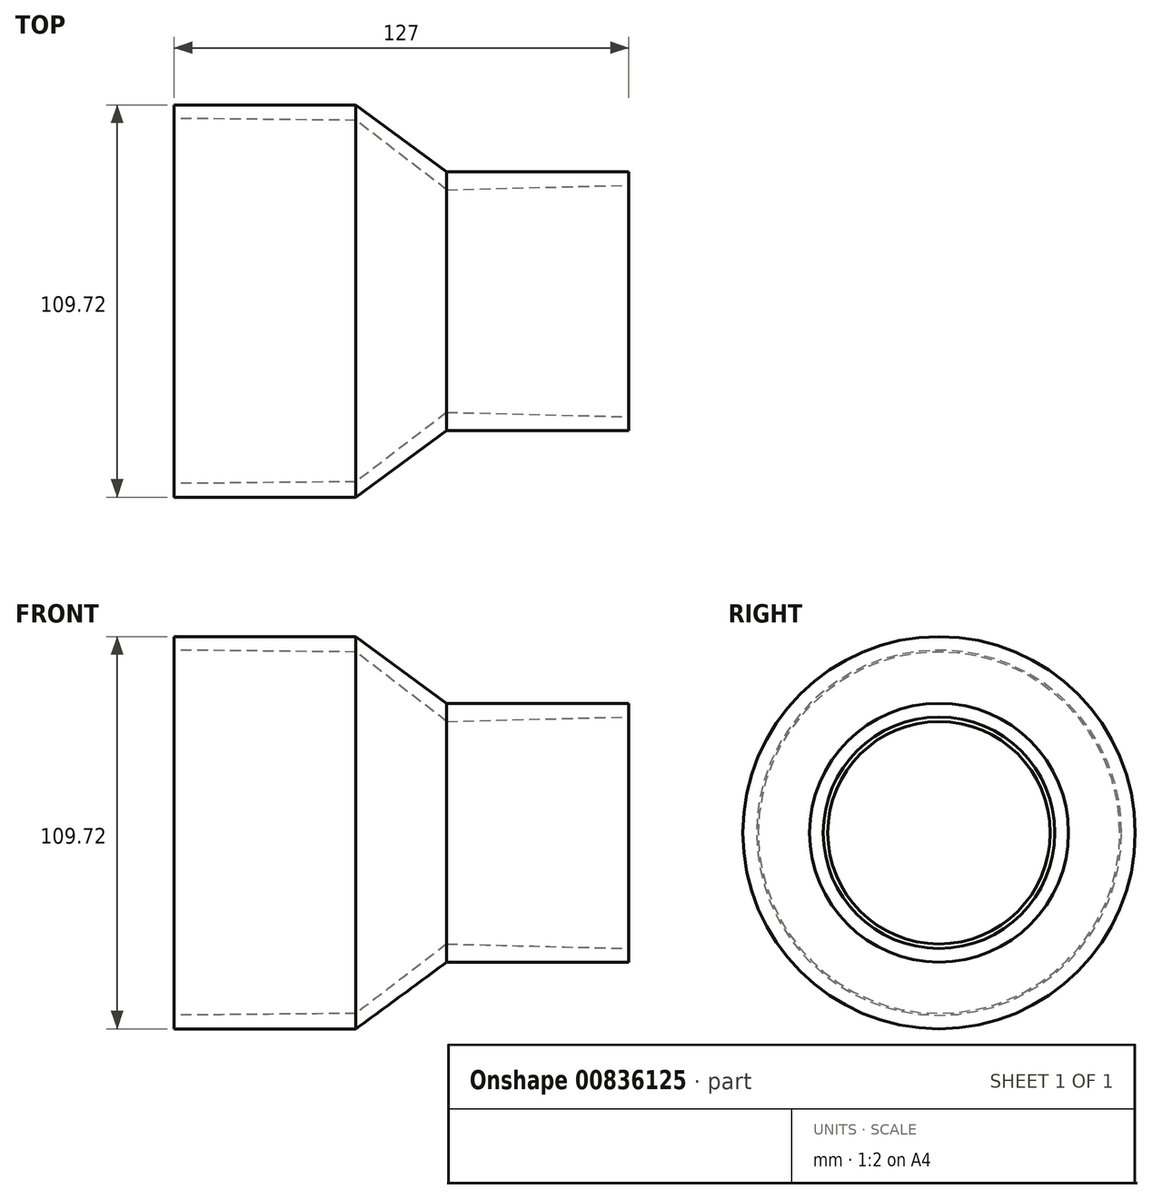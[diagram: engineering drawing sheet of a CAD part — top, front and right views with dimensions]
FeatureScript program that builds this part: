
annotation { "Feature Type Name" : "Feature", "Feature Type Description" : "" }
export const myFeature = defineFeature(function(context is Context, id is Id, definition is map)
    precondition{}
    {
        {
            var Q0;
            Q0=qCreatedBy(makeId("Front.planeOp"),FACE);
            var sketch = newSketch(context, id + "F0", { "sketchPlane" : qUnion([Q0])});
            skLineSegment(sketch, "E0", {"start": v(0, 0) * mm, "end": v(-90.9, 0) * mm, "construction": true});
            skLineSegment(sketch, "E1", {"start": v(0, 36.2) * mm, "end": v(50.8, 36.2) * mm});
            skLineSegment(sketch, "E2", {"start": v(50.8, 36.2) * mm, "end": v(50.8, 32.39) * mm});
            skLineSegment(sketch, "E3", {"start": v(50.8, 32.39) * mm, "end": v(0, 31.12) * mm});
            skLineSegment(sketch, "E4", {"start": v(0, 31.11) * mm, "end": v(-25.4, 50.55) * mm});
            skLineSegment(sketch, "E5", {"start": v(-25.4, 50.55) * mm, "end": v(-76.2, 51.05) * mm});
            skLineSegment(sketch, "E6", {"start": v(-76.2, 51.05) * mm, "end": v(-76.2, 54.86) * mm});
            skLineSegment(sketch, "E7", {"start": v(-76.2, 54.86) * mm, "end": v(-25.4, 54.86) * mm});
            skLineSegment(sketch, "E8", {"start": v(-25.4, 54.86) * mm, "end": v(0, 36.2) * mm});
            skPoint(sketch, "E9", {"position": v(25.4, 31.75) * mm});
            skPoint(sketch, "E10", {"position": v(-50.8, 50.8) * mm});
            skLineSegment(sketch, "E11", {"start": v(-25.4, 50.55) * mm, "end": v(-25.4, 54.86) * mm, "construction": true});
            skSolve(sketch);
        }
        {
            var Q0;
            Q0=qSketchRegion(id+"F0",true);
            var Q1;
            Q1=sQuery(id+"F0.wireOp",EDGE,"E0");
            revolve(context, id + "F1", {"surfaceOperationType" : NewSurfaceOperationType.NEW, "entities" : qUnion([Q0]), "axis" : qUnion([Q1]), "revolveType" : RevolveType.FULL});
        }
    });
